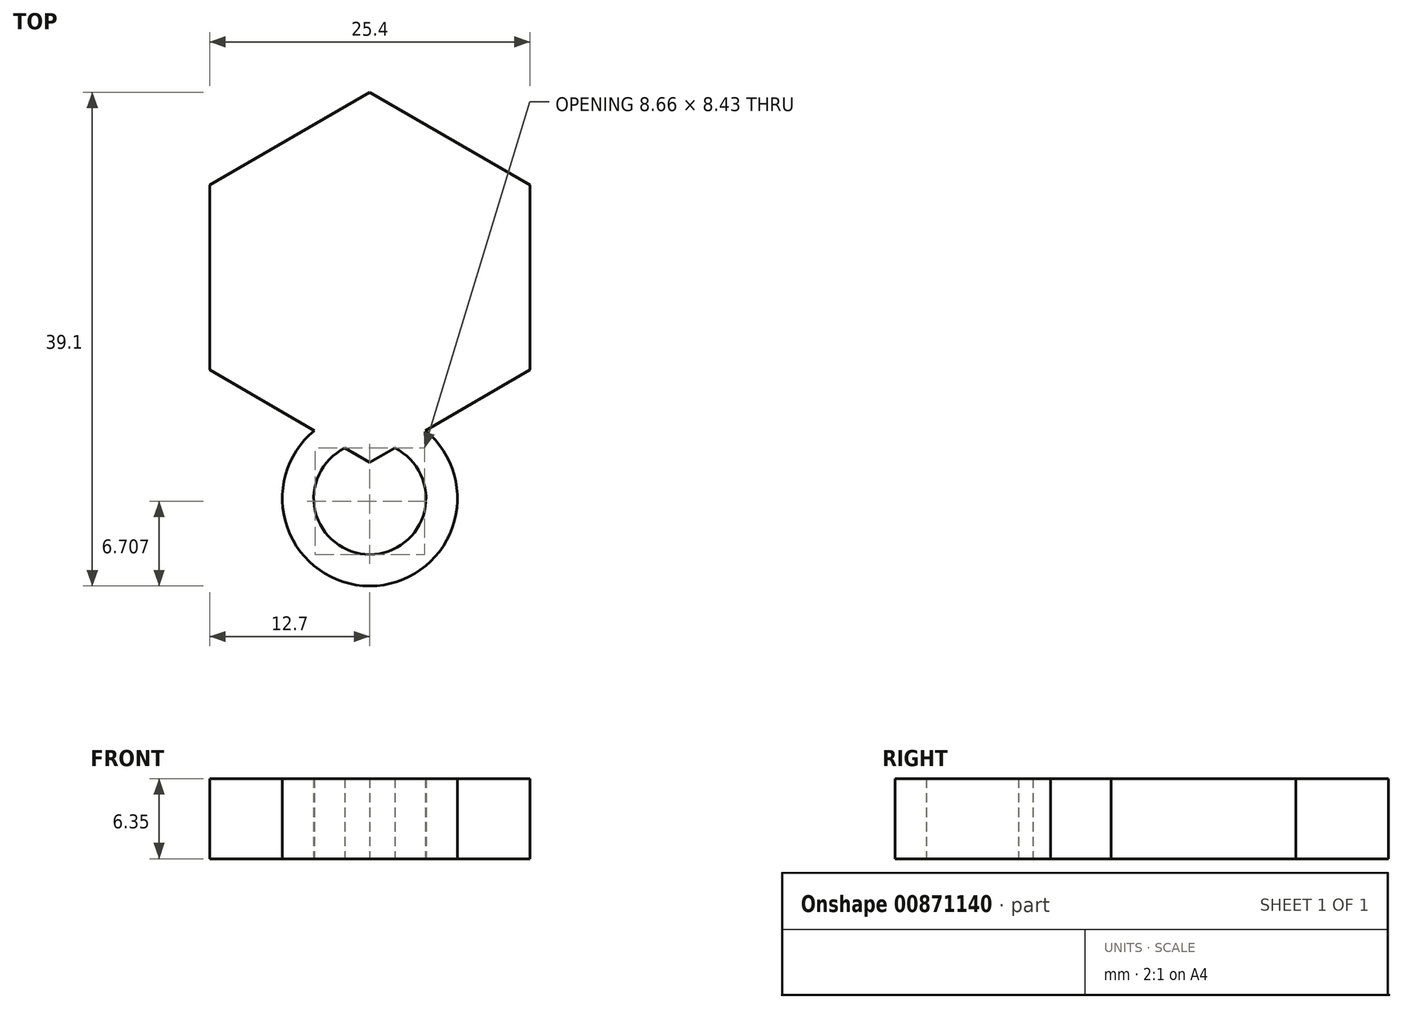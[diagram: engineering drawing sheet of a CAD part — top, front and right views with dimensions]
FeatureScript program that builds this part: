
annotation { "Feature Type Name" : "Feature", "Feature Type Description" : "" }
export const myFeature = defineFeature(function(context is Context, id is Id, definition is map)
    precondition{}
    {
        {
            var Q0;
            Q0=qCreatedBy(makeId("Top.planeOp"),FACE);
            var sketch = newSketch(context, id + "F0", { "sketchPlane" : qUnion([Q0])});
            skCircle(sketch, "E0.cCircle", {"center": v(0, 0) * mm, "radius": 12.7 * mm, "construction": true});
            skLineSegment(sketch, "E0.0", {"start": v(12.7, 7.33) * mm, "end": v(12.7, -7.33) * mm});
            skLineSegment(sketch, "E0.1", {"start": v(12.7, -7.33) * mm, "end": v(0, -14.66) * mm});
            skLineSegment(sketch, "E0.2", {"start": v(0, -14.66) * mm, "end": v(-12.7, -7.33) * mm});
            skLineSegment(sketch, "E0.3", {"start": v(-12.7, -7.33) * mm, "end": v(-12.7, 7.33) * mm});
            skLineSegment(sketch, "E0.4", {"start": v(-12.7, 7.33) * mm, "end": v(0, 14.66) * mm});
            skLineSegment(sketch, "E0.5", {"start": v(0, 14.66) * mm, "end": v(12.7, 7.33) * mm});
            skPoint(sketch, "E0.0.midPoint", {"position": v(12.7, 0) * mm});
            skSolve(sketch);
        }
        {
            var Q0;
            Q0=makeQuery(id+"F0.imprint","IMPRINT",FACE,{"disambiguationData":[TD([[makeQuery(id+"F0.imprint","IMPRINT",EDGE,{"derivedFrom":sQuery(id+"F0.wireOp",EDGE,"E0.0")}),-1.0]])]});
            extrude(context, id + "F1", {"entities" : qUnion([Q0]), "depth" : 6.35 * mm, "offsetDistance" : 25.4 * mm});
        }
        {
            var Q0;
            Q0=makeQuery(id+"F1.opExtrude","CAP_FACE",FACE,{"disambiguationData":[OSD([sQuery(id+"F0.wireOp",EDGE,"E0.0"),sQuery(id+"F0.wireOp",EDGE,"E0.1"),sQuery(id+"F0.wireOp",EDGE,"E0.2"),sQuery(id+"F0.wireOp",EDGE,"E0.3"),sQuery(id+"F0.wireOp",EDGE,"E0.4"),sQuery(id+"F0.wireOp",EDGE,"E0.5")])],"isStart":false});
            var sketch = newSketch(context, id + "F2", { "sketchPlane" : qUnion([Q0])});
            skSolve(sketch);
        }
        {
            var Q0;
            Q0=makeQuery(id+"F1.opExtrude","CAP_FACE",FACE,{"disambiguationData":[OSD([sQuery(id+"F0.wireOp",EDGE,"E0.0"),sQuery(id+"F0.wireOp",EDGE,"E0.1"),sQuery(id+"F0.wireOp",EDGE,"E0.2"),sQuery(id+"F0.wireOp",EDGE,"E0.3"),sQuery(id+"F0.wireOp",EDGE,"E0.4"),sQuery(id+"F0.wireOp",EDGE,"E0.5")])],"isStart":true});
            var sketch = newSketch(context, id + "F3", { "sketchPlane" : qUnion([Q0])});
            skCircle(sketch, "E1", {"center": v(0, 17.5) * mm, "radius": 6.94 * mm});
            skCircle(sketch, "E2", {"center": v(0, 17.5) * mm, "radius": 4.45 * mm});
            skSolve(sketch);
        }
        {
            var Q0;
            {var subQ0=sQuery(id+"F3.wireOp",EDGE,"E1");var subQ1=makeQuery(id+"F1.opExtrude","CAP_EDGE",EDGE,{"disambiguationData":[OSD([sQuery(id+"F0.wireOp",EDGE,"E0.1")])],"isStart":true});var subQ2=makeQuery(id+"F3.imprint","INTERSECT",VERTEX,{"derivedFrom":[subQ1,subQ0]});Q0=makeQuery(id+"F3.imprint","IMPRINT",FACE,{"disambiguationData":[TD([[makeQuery(id+"F3.imprint","IMPRINT",EDGE,{"disambiguationData":[TD([[subQ2,-1.0]])],"derivedFrom":subQ0}),1.0]])]});}
            var Q1;
            Q1=makeQuery(id+"F1.opExtrude","CAP_FACE",FACE,{"disambiguationData":[OSD([sQuery(id+"F0.wireOp",EDGE,"E0.0"),sQuery(id+"F0.wireOp",EDGE,"E0.1"),sQuery(id+"F0.wireOp",EDGE,"E0.2"),sQuery(id+"F0.wireOp",EDGE,"E0.3"),sQuery(id+"F0.wireOp",EDGE,"E0.4"),sQuery(id+"F0.wireOp",EDGE,"E0.5")])],"isStart":false});
            extrude(context, id + "F4", {"entities" : qUnion([Q0]), "operationType" : NewBodyOperationType.ADD, "endBound" : BoundingType.UP_TO_SURFACE, "oppositeDirection" : true, "depth" : 6.35 * mm, "endBoundEntityFace" : qUnion([Q1]), "offsetDistance" : 25.4 * mm});
        }
    });
